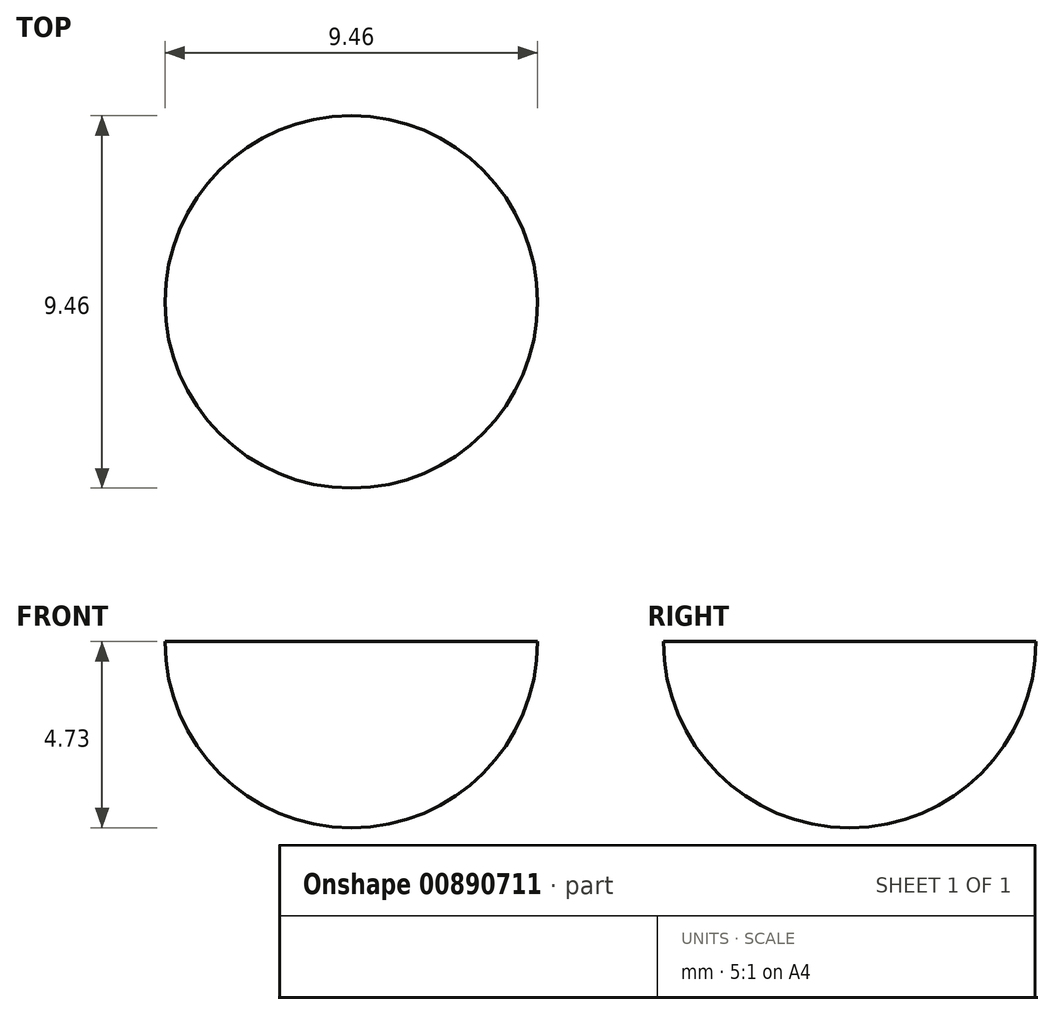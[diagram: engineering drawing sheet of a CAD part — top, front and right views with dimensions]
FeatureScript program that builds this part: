
annotation { "Feature Type Name" : "Feature", "Feature Type Description" : "" }
export const myFeature = defineFeature(function(context is Context, id is Id, definition is map)
    precondition{}
    {
        {
            var Q0;
            Q0=qCreatedBy(makeId("Top.planeOp"),FACE);
            var sketch = newSketch(context, id + "F0", { "sketchPlane" : qUnion([Q0])});
            skCircle(sketch, "E0", {"center": v(0, 0) * mm, "radius": 5 * mm});
            skArc(sketch, "E1", {"start": v(0, 4.73) * mm, "mid": v(-4.73, 0) * mm, "end": v(0, -4.73) * mm});
            skLineSegment(sketch, "E2", {"start": v(0, 4.73) * mm, "end": v(0, -4.73) * mm});
            skSolve(sketch);
        }
        {
            var Q0;
            Q0 = qSketchRegion(id + "F0", true);
            var Q1;
            Q1=sQuery(id+"F0.wireOp",EDGE,"E1");
            var Q2;
            Q2=sQuery(id+"F0.wireOp",EDGE,"E2");
            revolve(context, id + "F1", {"bodyType" : ToolBodyType.SURFACE, "surfaceOperationType" : NewSurfaceOperationType.NEW, "entities" : qUnion([Q0]), "surfaceEntities" : qUnion([Q1]), "axis" : qUnion([Q2]), "revolveType" : RevolveType.ONE_DIRECTION, "angle" : 180 * degree});
        }
    });
